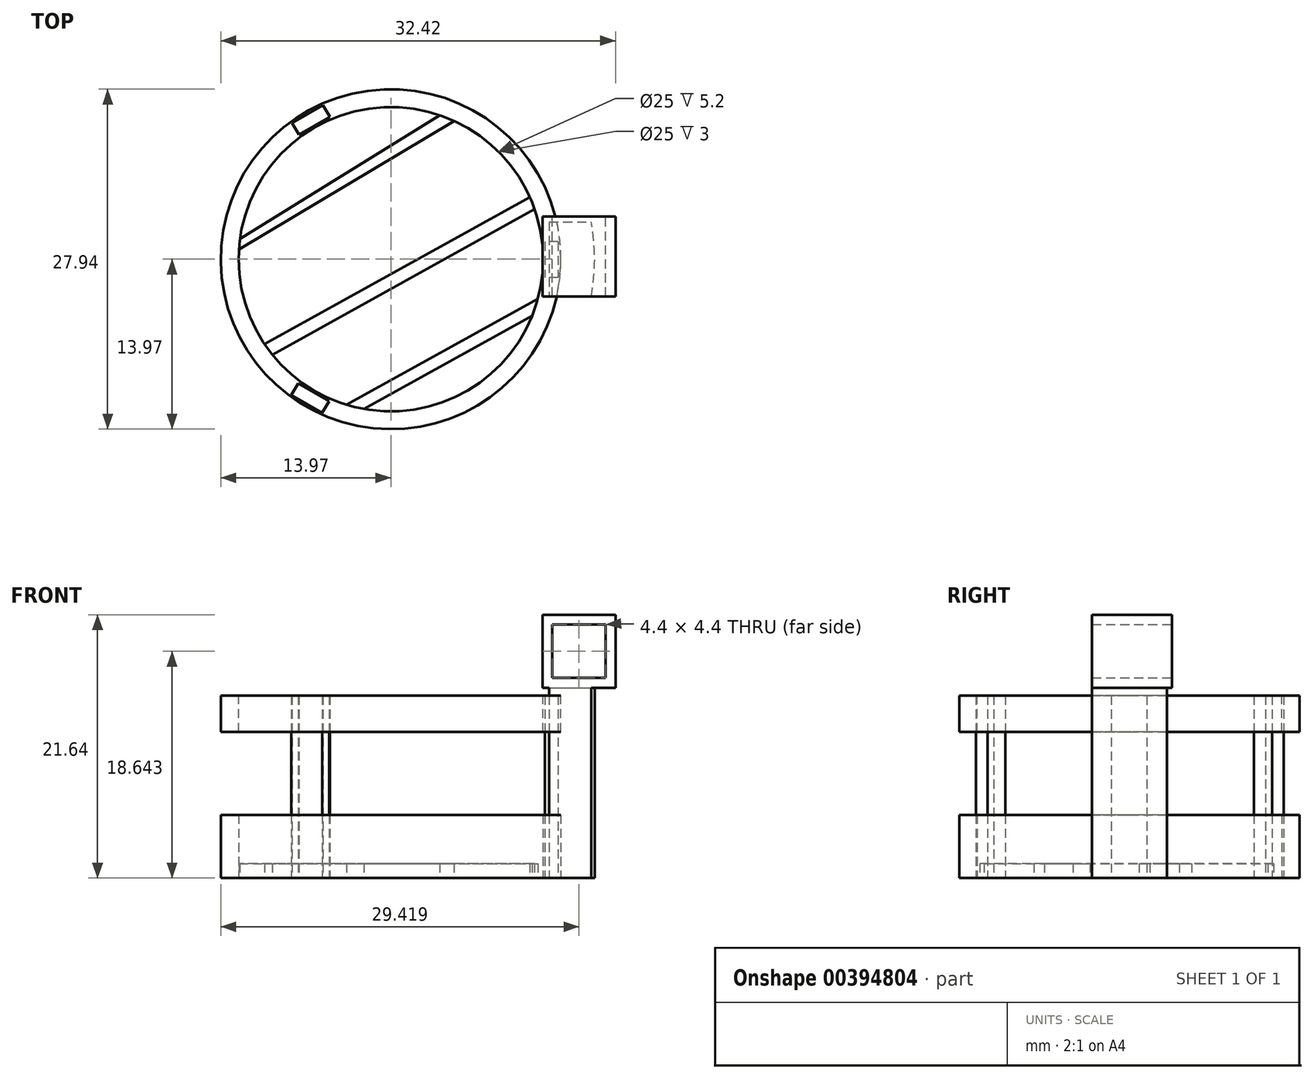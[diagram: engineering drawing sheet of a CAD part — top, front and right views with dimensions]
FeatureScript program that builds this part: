
annotation { "Feature Type Name" : "Feature", "Feature Type Description" : "" }
export const myFeature = defineFeature(function(context is Context, id is Id, definition is map)
    precondition{}
    {
        {
            var Q0;
            Q0=qCreatedBy(makeId("Top.planeOp"),FACE);
            var sketch = newSketch(context, id + "F0", { "sketchPlane" : qUnion([Q0])});
            skCircle(sketch, "E0", {"center": v(0, 0) * mm, "radius": 12.5 * mm});
            skCircle(sketch, "E1", {"center": v(0, 0) * mm, "radius": 13.97 * mm});
            skSolve(sketch);
        }
        {
            var Q0;
            Q0 = qSketchRegion(id + "F0", true);
            extrude(context, id + "F1", {"entities" : qUnion([Q0]), "depth" : 5.2 * mm});
        }
        {
            var Q0;
            Q0=qCreatedBy(makeId("Top.planeOp"),FACE);
            var sketch = newSketch(context, id + "F2", { "sketchPlane" : qUnion([Q0])});
            skLineSegment(sketch, "E2", {"start": v(4.63, 12.23) * mm, "end": v(-13.4, 1.05) * mm});
            skLineSegment(sketch, "E3", {"start": v(-13.4, 1.05) * mm, "end": v(-13.4, 0.25) * mm});
            skLineSegment(sketch, "E4", {"start": v(-13.4, 0.25) * mm, "end": v(5.8, 11.72) * mm});
            skLineSegment(sketch, "E5", {"start": v(5.8, 11.72) * mm, "end": v(4.63, 12.23) * mm});
            skLineSegment(sketch, "E6", {"start": v(-11.18, -7.44) * mm, "end": v(11.87, 5.35) * mm});
            skLineSegment(sketch, "E7", {"start": v(11.87, 5.35) * mm, "end": v(12.38, 4.42) * mm});
            skLineSegment(sketch, "E8", {"start": v(12.38, 4.42) * mm, "end": v(-10.66, -8.36) * mm});
            skLineSegment(sketch, "E9", {"start": v(-10.66, -8.36) * mm, "end": v(-11.18, -7.44) * mm});
            skLineSegment(sketch, "E10", {"start": v(-4.98, -12.7) * mm, "end": v(13.07, -2.69) * mm});
            skLineSegment(sketch, "E11", {"start": v(13.07, -2.69) * mm, "end": v(12.41, -4.2) * mm});
            skLineSegment(sketch, "E12", {"start": v(12.41, -4.2) * mm, "end": v(-3.93, -13.26) * mm});
            skLineSegment(sketch, "E13", {"start": v(-3.93, -13.26) * mm, "end": v(-4.98, -12.7) * mm});
            skSolve(sketch);
        }
        {
            var Q0;
            Q0 = qSketchRegion(id + "F2", true);
            extrude(context, id + "F3", {"entities" : qUnion([Q0]), "operationType" : NewBodyOperationType.ADD, "depth" : 1.2 * mm});
        }
        {
            var Q0;
            Q0=qCreatedBy(makeId("Top.planeOp"),FACE);
            cPlane(context, id + "F4", {"entities" : qUnion([Q0]), "cplaneType" : CPlaneType.OFFSET, "offset" : 15 * mm, "width" : 150 * mm, "height" : 150 * mm});
        }
        {
            var Q0;
            Q0=qCreatedBy(id+"F4.planeOp",FACE);
            var sketch = newSketch(context, id + "F5", { "sketchPlane" : qUnion([Q0])});
            skCircle(sketch, "E14.0.0", {"center": v(0, 0) * mm, "radius": 13.97 * mm});
            skCircle(sketch, "E15.0", {"center": v(0, 0) * mm, "radius": 12.5 * mm});
            skSolve(sketch);
        }
        {
            var Q0;
            Q0 = qSketchRegion(id + "F5", true);
            extrude(context, id + "F6", {"entities" : qUnion([Q0]), "oppositeDirection" : true, "depth" : 3 * mm});
        }
        {
            var Q0;
            Q0=qCreatedBy(makeId("Top.planeOp"),FACE);
            var sketch = newSketch(context, id + "F7", { "sketchPlane" : qUnion([Q0])});
            skLineSegment(sketch, "E16.bottom", {"start": v(13.74, 1.43) * mm, "end": v(12.64, 1.43) * mm});
            skLineSegment(sketch, "E16.top", {"start": v(13.74, -1.5) * mm, "end": v(12.64, -1.5) * mm});
            skLineSegment(sketch, "E16.left", {"start": v(13.74, 1.43) * mm, "end": v(13.74, -1.5) * mm});
            skLineSegment(sketch, "E16.right", {"start": v(12.64, 1.43) * mm, "end": v(12.64, -1.5) * mm});
            skLineSegment(sketch, "E17.1.0", {"start": v(-8.1, 11.19) * mm, "end": v(-7.56, 10.23) * mm});
            skLineSegment(sketch, "E17.1.1", {"start": v(-5.57, 12.65) * mm, "end": v(-5.02, 11.7) * mm});
            skLineSegment(sketch, "E17.1.2", {"start": v(-8.1, 11.19) * mm, "end": v(-5.57, 12.65) * mm});
            skLineSegment(sketch, "E17.1.3", {"start": v(-7.56, 10.23) * mm, "end": v(-5.02, 11.7) * mm});
            skLineSegment(sketch, "E17.2.0", {"start": v(-5.63, -12.62) * mm, "end": v(-5.08, -11.66) * mm});
            skLineSegment(sketch, "E17.2.1", {"start": v(-8.17, -11.15) * mm, "end": v(-7.62, -10.2) * mm});
            skLineSegment(sketch, "E17.2.2", {"start": v(-5.63, -12.62) * mm, "end": v(-8.17, -11.15) * mm});
            skLineSegment(sketch, "E17.2.3", {"start": v(-5.08, -11.66) * mm, "end": v(-7.62, -10.2) * mm});
            skPoint(sketch, "E17.center", {"position": v(0, 0) * mm});
            skSolve(sketch);
        }
        {
            var Q0;
            Q0 = qSketchRegion(id + "F7", true);
            var Q1;
            Q1=makeQuery(id+"F6.opExtrude","CAP_FACE",FACE,{"disambiguationData":[OSD([sQuery(id+"F5.wireOp",EDGE,"E14.0.0"),sQuery(id+"F5.wireOp",EDGE,"E15.0")])],"isStart":true});
            extrude(context, id + "F8", {"entities" : qUnion([Q0]), "endBound" : BoundingType.UP_TO_SURFACE, "endBoundEntityFace" : qUnion([Q1]), "depth" : 25 * mm});
        }
        {
            var Q0;
            Q0=qCreatedBy(makeId("Top.planeOp"),FACE);
            var sketch = newSketch(context, id + "F9", { "sketchPlane" : qUnion([Q0])});
            skArc(sketch, "E18", {"start": v(16.45, -3.07) * mm, "mid": v(16.73, 0) * mm, "end": v(16.45, 3.07) * mm});
            skLineSegment(sketch, "E19", {"start": v(16.45, 3.07) * mm, "end": v(13, 3.07) * mm});
            skLineSegment(sketch, "E20", {"start": v(13, 3.07) * mm, "end": v(13, 0) * mm});
            skLineSegment(sketch, "E21.MirrorCS", {"start": v(16.45, -3.07) * mm, "end": v(13, -3.07) * mm});
            skLineSegment(sketch, "E22.MirrorCS", {"start": v(13, -3.07) * mm, "end": v(13, 0) * mm});
            skSolve(sketch);
        }
        {
            var Q0;
            Q0 = qSketchRegion(id + "F9", true);
            extrude(context, id + "F10", {"entities" : qUnion([Q0]), "depth" : 17.6 * mm});
        }
        {
            var Q0;
            Q0=qCreatedBy(makeId("Front.planeOp"),FACE);
            var sketch = newSketch(context, id + "F11", { "sketchPlane" : qUnion([Q0])});
            skLineSegment(sketch, "E23.bottom", {"start": v(12.45, 21.64) * mm, "end": v(18.45, 21.64) * mm});
            skLineSegment(sketch, "E23.top", {"start": v(12.45, 15.64) * mm, "end": v(18.45, 15.64) * mm});
            skLineSegment(sketch, "E23.left", {"start": v(12.45, 21.64) * mm, "end": v(12.45, 15.64) * mm});
            skLineSegment(sketch, "E23.right", {"start": v(18.45, 21.64) * mm, "end": v(18.45, 15.64) * mm});
            skSolve(sketch);
        }
        {
            var Q0;
            Q0 = qSketchRegion(id + "F11", true);
            var Q1;
            Q1=makeQuery(id+"F10.opExtrude","SWEPT_FACE",FACE,{"disambiguationData":[OSD([sQuery(id+"F9.wireOp",EDGE,"E21.MirrorCS")])]});
            extrude(context, id + "F12", {"entities" : qUnion([Q0]), "operationType" : NewBodyOperationType.ADD, "endBound" : BoundingType.UP_TO_SURFACE, "endBoundEntityFace" : qUnion([Q1]), "depth" : 6.1 * mm});
        }
        {
            var Q0;
            Q0=qCreatedBy(makeId("Front.planeOp"),FACE);
            var sketch = newSketch(context, id + "F13", { "sketchPlane" : qUnion([Q0])});
            skLineSegment(sketch, "E24.0", {"start": v(12.45, 21.64) * mm, "end": v(12.45, 15.64) * mm});
            skLineSegment(sketch, "E25.0", {"start": v(12.45, 21.64) * mm, "end": v(18.45, 21.64) * mm});
            skLineSegment(sketch, "E26.0", {"start": v(18.45, 21.64) * mm, "end": v(18.45, 15.64) * mm});
            skLineSegment(sketch, "E27", {"start": v(12.45, 15.64) * mm, "end": v(18.45, 15.64) * mm});
            skSolve(sketch);
        }
        {
            var Q0;
            Q0=makeQuery(id+"F13.imprint","IMPRINT",FACE,{"disambiguationData":[TD([[makeQuery(id+"F13.imprint","IMPRINT",EDGE,{"derivedFrom":sQuery(id+"F13.wireOp",EDGE,"E24.0")}),1.0]])]});
            var Q1;
            Q1 = qSketchRegion(id + "F13", true);
            extrude(context, id + "F14", {"entities" : qUnion([Q0, Q1]), "operationType" : NewBodyOperationType.ADD, "oppositeDirection" : true, "depth" : 3.5 * mm});
        }
        {
            var Q0;
            Q0=makeQuery(id+"F14.opExtrude","CAP_FACE",FACE,{"disambiguationData":[OSD([sQuery(id+"F13.wireOp",EDGE,"E24.0"),sQuery(id+"F13.wireOp",EDGE,"E25.0"),sQuery(id+"F13.wireOp",EDGE,"E26.0"),sQuery(id+"F13.wireOp",EDGE,"E27")])],"isStart":false});
            var sketch = newSketch(context, id + "F15", { "sketchPlane" : qUnion([Q0])});
            skLineSegment(sketch, "E28.0", {"start": v(-13.25, 16.44) * mm, "end": v(-13.25, 20.84) * mm});
            skLineSegment(sketch, "E28.1", {"start": v(-17.65, 16.44) * mm, "end": v(-13.25, 16.44) * mm});
            skLineSegment(sketch, "E28.2", {"start": v(-17.65, 20.84) * mm, "end": v(-17.65, 16.44) * mm});
            skLineSegment(sketch, "E28.3", {"start": v(-13.25, 20.84) * mm, "end": v(-17.65, 20.84) * mm});
            skSolve(sketch);
        }
        {
            var Q0;
            Q0 = qSketchRegion(id + "F15", true);
            extrude(context, id + "F16", {"entities" : qUnion([Q0]), "operationType" : NewBodyOperationType.REMOVE, "oppositeDirection" : true, "depth" : 25 * mm});
        }
    });
